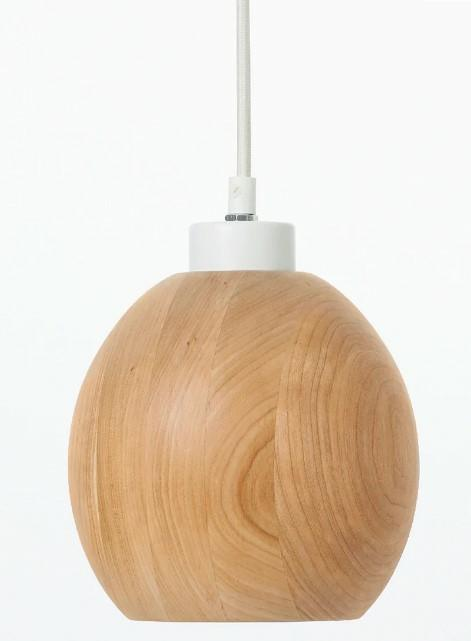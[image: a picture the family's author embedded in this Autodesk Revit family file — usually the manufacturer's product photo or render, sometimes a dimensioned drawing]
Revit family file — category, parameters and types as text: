
# Revit family: Bommel Bulb Lamp - Birch
name_source: partatom
category: Lighting Fixtures
units: mm (PartAtom-declared; Revit-internal decimal feet)

## family parameters
Always vertical = Yes
Cut with Voids When Loaded = No
Host = Ceiling
Light Source = Yes
OmniClass Number = 23.80.70.11
OmniClass Title = Luminaries for Internal Lighting
Part Type = Normal
Room Calculation Point = No
Round Connector Dimension = Use Diameter
Shared = No

## types (1)
- Bommel Bulb Lamp - Birch
    Area = 0
    BarCode = <None>
    Color Filter = 16777215
    Default Elevation = 0' - 0"
    Dimming Lamp Color Temperature Shift = <None>
    Height = 0
    IsExtendedWarranty = 0
    Light Source Symbol Length = 10' - 0"
    NominalHeight = 0
    NominalLength = 0
    NominalWidth = 0
    ReplacementCost = 0
    Spot Beam Angle = 30.00°
    Spot Field Angle = 90.00°
    Tilt Angle = 90.00°
    WarrantyDurationLabor = 0
    WarrantyDurationParts = 0
    WarrantyPeriod = 0
    Width = 0

## geometry (parser evidence)
native form markers: Sweep x2
no freeform markers — native parametric forms only
